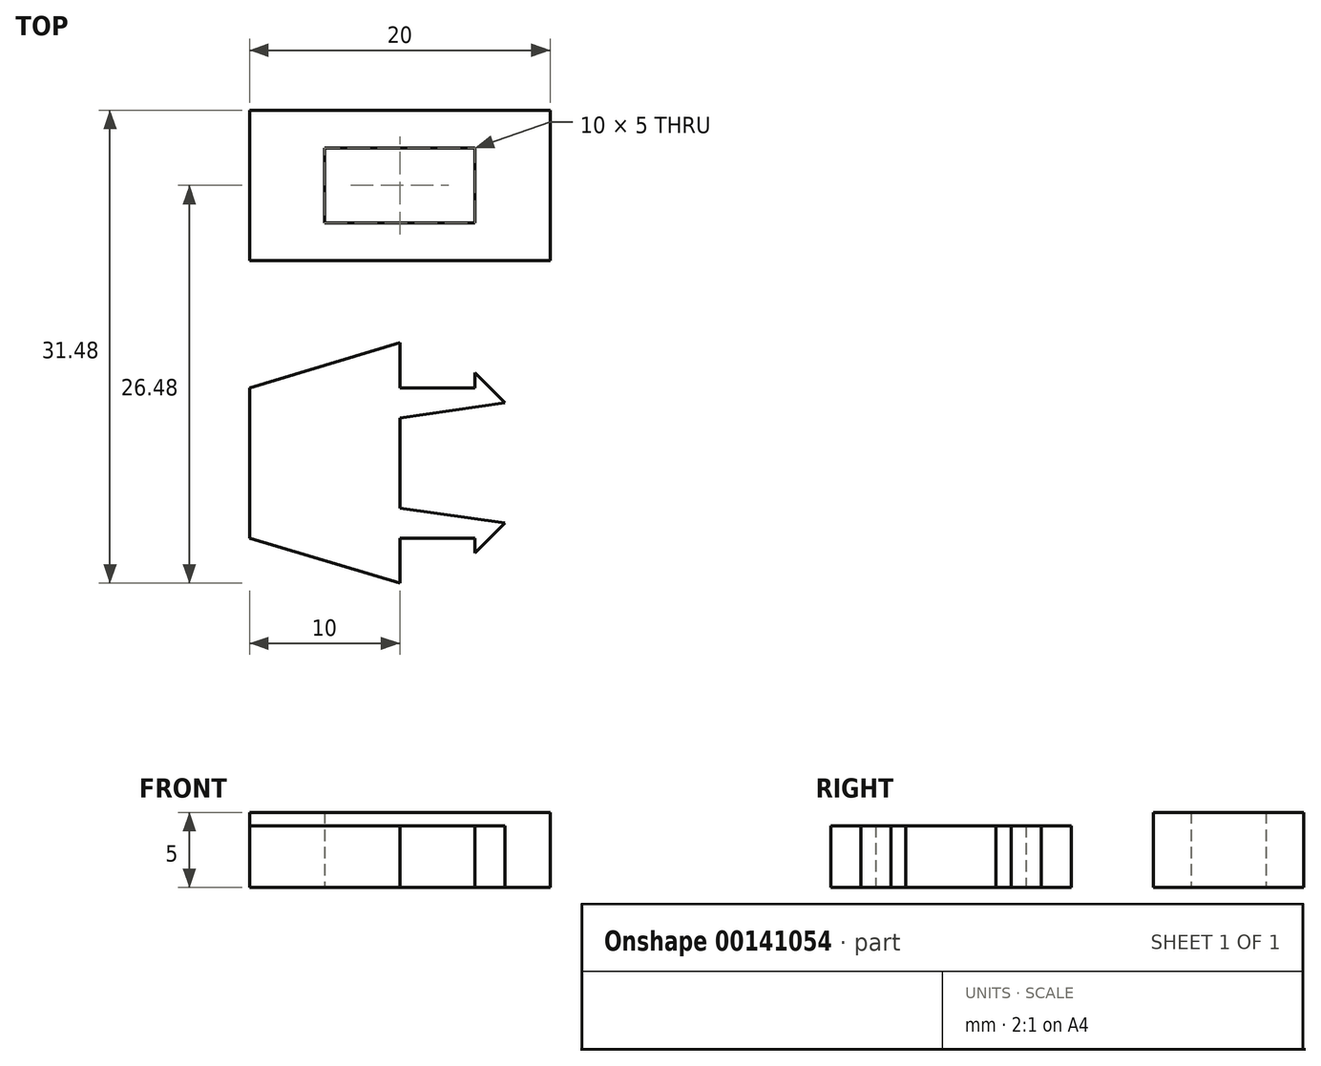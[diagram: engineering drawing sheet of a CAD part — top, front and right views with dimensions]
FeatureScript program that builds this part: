
annotation { "Feature Type Name" : "Feature", "Feature Type Description" : "" }
export const myFeature = defineFeature(function(context is Context, id is Id, definition is map)
    precondition{}
    {
        {
            var Q0;
            Q0=qCreatedBy(makeId("Top.planeOp"),FACE);
            var sketch = newSketch(context, id + "F0", { "sketchPlane" : qUnion([Q0])});
            skLineSegment(sketch, "E0.bottom", {"start": v(0, 0) * mm, "end": v(20, 0) * mm});
            skLineSegment(sketch, "E0.top", {"start": v(0, 10) * mm, "end": v(20, 10) * mm});
            skLineSegment(sketch, "E0.left", {"start": v(0, 0) * mm, "end": v(0, 10) * mm});
            skLineSegment(sketch, "E0.right", {"start": v(20, 0) * mm, "end": v(20, 10) * mm});
            skSolve(sketch);
        }
        {
            var Q0;
            Q0=makeQuery(id+"F0.imprint","IMPRINT",FACE,{"disambiguationData":[TD([[makeQuery(id+"F0.imprint","IMPRINT",EDGE,{"derivedFrom":sQuery(id+"F0.wireOp",EDGE,"E0.bottom")}),1.0]])]});
            var sketch = newSketch(context, id + "F1", { "sketchPlane" : qUnion([Q0])});
            skLineSegment(sketch, "E1.bottom", {"start": v(5, 7.5) * mm, "end": v(15, 7.5) * mm});
            skLineSegment(sketch, "E1.top", {"start": v(5, 2.5) * mm, "end": v(15, 2.5) * mm});
            skLineSegment(sketch, "E1.left", {"start": v(5, 7.5) * mm, "end": v(5, 2.5) * mm});
            skLineSegment(sketch, "E1.right", {"start": v(15, 7.5) * mm, "end": v(15, 2.5) * mm});
            skSolve(sketch);
        }
        {
            var Q0;
            Q0=qSketchRegion(id+"F0",true);
            extrude(context, id + "F2", {"entities" : qUnion([Q0]), "depth" : 5 * mm});
        }
        {
            var Q0;
            Q0=qSketchRegion(id+"F1",true);
            extrude(context, id + "F3", {"entities" : qUnion([Q0]), "operationType" : NewBodyOperationType.REMOVE, "endBound" : BoundingType.THROUGH_ALL, "depth" : 25 * mm});
        }
        {
            var Q0;
            Q0=qCreatedBy(makeId("Top.planeOp"),FACE);
            var sketch = newSketch(context, id + "F4", { "sketchPlane" : qUnion([Q0])});
            skLineSegment(sketch, "E2", {"start": v(15, -8.48) * mm, "end": v(15, -7.48) * mm});
            skLineSegment(sketch, "E3", {"start": v(15, -7.48) * mm, "end": v(17, -9.48) * mm});
            skLineSegment(sketch, "E4", {"start": v(17, -9.48) * mm, "end": v(10, -10.48) * mm});
            skLineSegment(sketch, "E5", {"start": v(10, -10.48) * mm, "end": v(10, -16.48) * mm});
            skLineSegment(sketch, "E6", {"start": v(10, -16.48) * mm, "end": v(17, -17.48) * mm});
            skLineSegment(sketch, "E7", {"start": v(17, -17.48) * mm, "end": v(15, -19.48) * mm});
            skLineSegment(sketch, "E8", {"start": v(15, -19.48) * mm, "end": v(15, -18.48) * mm});
            skLineSegment(sketch, "E9", {"start": v(0, -18.48) * mm, "end": v(0, -8.48) * mm});
            skLineSegment(sketch, "E10", {"start": v(0, -8.48) * mm, "end": v(10, -5.48) * mm});
            skLineSegment(sketch, "E11", {"start": v(10, -5.48) * mm, "end": v(10, -8.48) * mm});
            skLineSegment(sketch, "E12", {"start": v(0, -18.48) * mm, "end": v(10, -21.48) * mm});
            skLineSegment(sketch, "E13", {"start": v(10, -21.48) * mm, "end": v(10, -18.48) * mm});
            skLineSegment(sketch, "E14", {"start": v(10, -8.48) * mm, "end": v(15, -8.48) * mm});
            skLineSegment(sketch, "E15", {"start": v(10, -18.48) * mm, "end": v(15, -18.48) * mm});
            skSolve(sketch);
        }
        {
            var Q0;
            Q0=qSketchRegion(id+"F4",true);
            extrude(context, id + "F5", {"entities" : qUnion([Q0]), "depth" : 4.1 * mm});
        }
    });
